# Revit family: PRD_AR_PprTwlDspnsrs_STRATOSElectronicPaperTowelDispenser_STR630
name_source: partatom
category: Specialty Equipment
units: mm (PartAtom-declared; Revit-internal decimal feet)

## family parameters
Cut with Voids When Loaded = No
Host = Face
OmniClass Number = 23.40.20.21.17
OmniClass Title = Paper Towel Dispensers, Disposal Units
Part Type = Normal
Room Calculation Point = No
Round Connector Dimension = Use Diameter
Shared = No

## types (1)
- STR630
    AssetType = Fixed
    BIMObjectName = PRD_AR_PaperTowelDispensers_STRATOSElectronicPaperTowelDispenser_STR630
    Category = Pr_40_70_22_62, Paper Towel Dispensers
    Default Elevation = 850 mm  [stored 2.78871 ft]
    Description = STRATOS electronic paper towel dispenser for wall mounting, stainless steel, surface satin finished, material thickness 1.5 mm, curved front with inspection window, cylinder lock with key, non-contact paper dispensing via infrared sensor, integrated tear-off edge, including four 1.5 V (=6 V) batteries type D, easy paper roll change, suitable for rolls with a width of 190-205 mm and a core of 35 mm, maximum diameter approx. 200 mm, paper length adjustable in three lengths to 200, 250 and 300 mm, including mounting material.
    DispenserMaterial = PRD_AR_StainlessSteel_SatinFinished
    DurationUnit = year
    Features = stainless steel, surface satin finished
    FillingQuantity = 1
    FillingQuantityUom = Rolls
    Finish = satin finished
    GrossWeight = 7.85 kg
    IfcExportAs = IfcFurnitureType
    IfcExportType = USERDEFINIED
    IntegralAccessories = incl. stainless steel screws and dowels
    IsBuiltIn = TRUE
    Lock = Key-lock
    MainColor = stainless steel
    Manufacturer = KWC Group Management AG
    ManufacturerName = KWC Group Management AG
    ManufacturerURL = www.kwc-professional.com
    Material = stainless steel
    MaterialCode = 1.4301
    MaterialThickness = 1.50 mm
    MaximumDepthDiameterOfConsumable = 220.00 mm
    MaximumDepthOfConsumable = 205.00 mm
    Model = STR630
    ModelNumber = 3600008885
    ModelReference = STR630
    NBSDescription = Paper towel dispensers
    NBSReference = 45-35-72/344
    Name = STRATOS Electronic Paper Towel Dispenser STR630
    NetWeight = 6.85 kg
    NominalDepth = 234 mm  [stored 0.767717 ft]
    NominalHeight = 383 mm  [stored 1.25656 ft]
    NominalWidth = 300 mm  [stored 0.984252 ft]
    NumberOfBatteries = 4
    ProductInformation = http://pim.kwc.com
    Size = 300 x 383 x 234 mm
    Style = dispenser
    TypeOfBatteries = D Mono battery 1.5 V
    TypeOfConsumable = Paper roll
    TypeOfFixing = Screw
    TypeOfMounting = Wall mounting
    TypeOfOperation = Sensor operation
    URL = www.kwc-professional.com
    Uniclass2015Code = Pr_40_70_22_62
    Uniclass2015Title = Paper towel dispensers
    Uniclass2015Version = Products v1.10
    Version = 1
    WarrantyDurationUnit = year

note: [stored X ft] marks values corroborated as IEEE doubles in the binary element streams (Revit-internal decimal feet)

## geometry (parser evidence)
native form markers: Sweep x4
no freeform markers — native parametric forms only
